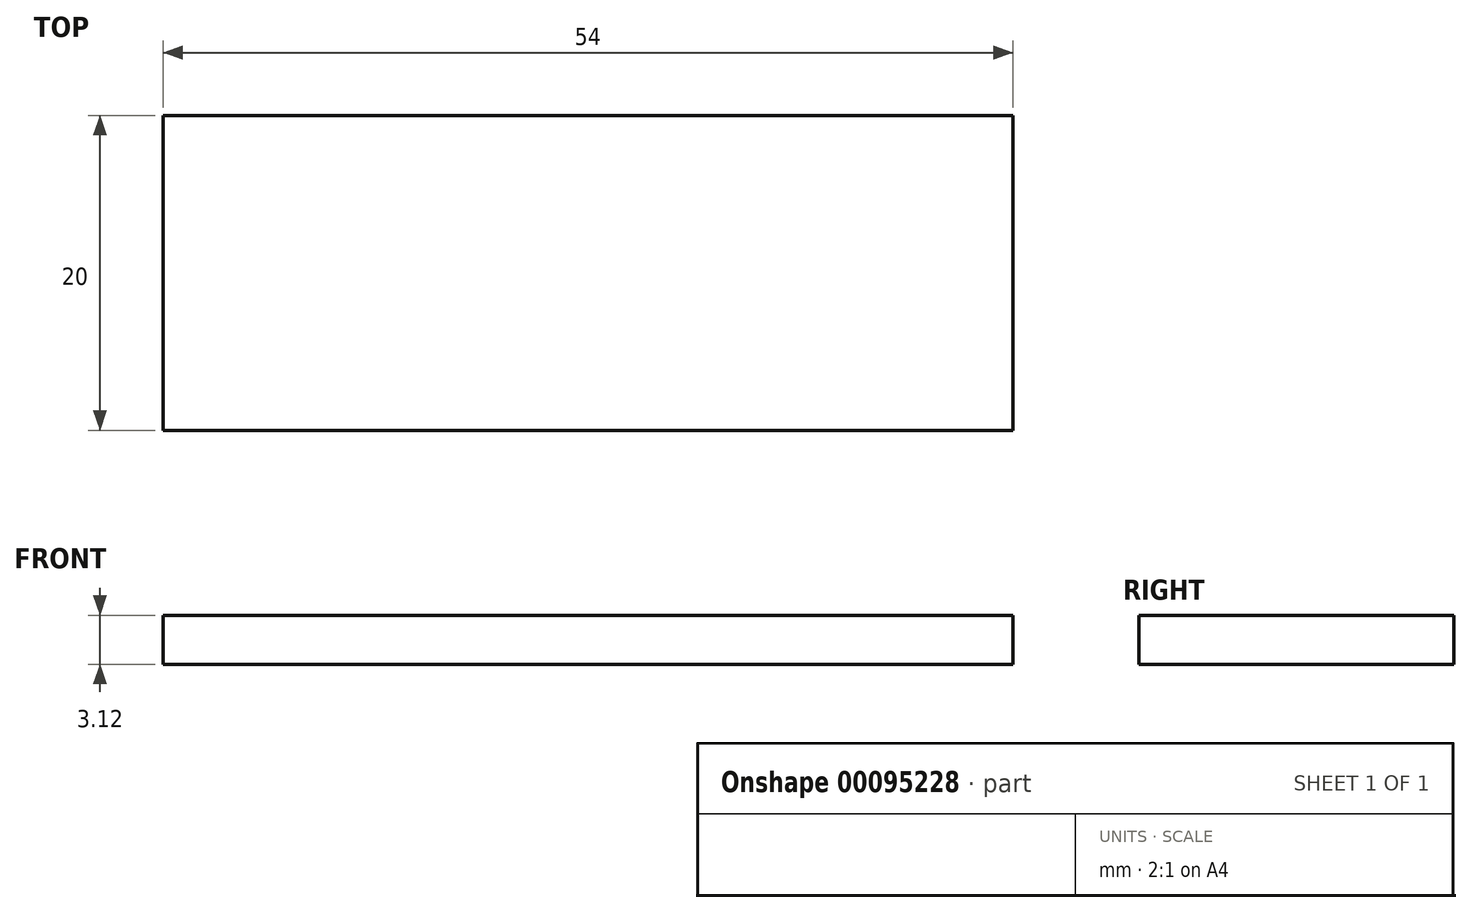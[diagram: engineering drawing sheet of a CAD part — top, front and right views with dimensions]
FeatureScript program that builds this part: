
annotation { "Feature Type Name" : "Feature", "Feature Type Description" : "" }
export const myFeature = defineFeature(function(context is Context, id is Id, definition is map)
    precondition{}
    {
        {
            var Q0;
            Q0=qCreatedBy(makeId("Top.planeOp"),FACE);
            var sketch = newSketch(context, id + "F0", { "sketchPlane" : qUnion([Q0])});
            skLineSegment(sketch, "E0.bottom", {"start": v(27, 10) * mm, "end": v(-27, 10) * mm});
            skLineSegment(sketch, "E0.top", {"start": v(27, -10) * mm, "end": v(-27, -10) * mm});
            skLineSegment(sketch, "E0.left", {"start": v(27, 10) * mm, "end": v(27, -10) * mm});
            skLineSegment(sketch, "E0.right", {"start": v(-27, 10) * mm, "end": v(-27, -10) * mm});
            skPoint(sketch, "E0.middle", {"position": v(0, 0) * mm});
            skSolve(sketch);
        }
        {
            var Q0;
            Q0=makeQuery(id+"F0.imprint","IMPRINT",FACE,{"disambiguationData":[TD([[makeQuery(id+"F0.imprint","IMPRINT",EDGE,{"derivedFrom":sQuery(id+"F0.wireOp",EDGE,"E0.bottom")}),1.0]])]});
            extrude(context, id + "F1", {"entities" : qUnion([Q0]), "depth" : 3.12 * mm});
        }
    });
